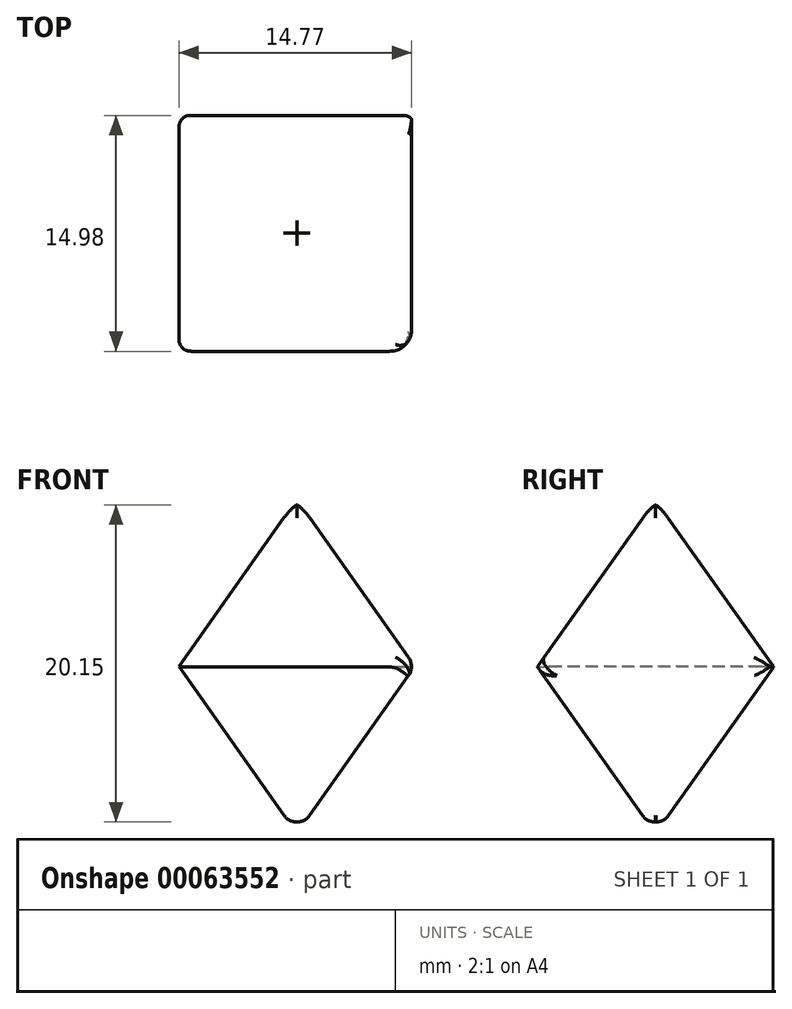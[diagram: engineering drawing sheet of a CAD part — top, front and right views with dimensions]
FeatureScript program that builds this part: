
annotation { "Feature Type Name" : "Feature", "Feature Type Description" : "" }
export const myFeature = defineFeature(function(context is Context, id is Id, definition is map)
    precondition{}
    {
        {
            var Q0;
            Q0=qCreatedBy(makeId("Top.planeOp"),FACE);
            var sketch = newSketch(context, id + "F0", { "sketchPlane" : qUnion([Q0])});
            skLineSegment(sketch, "E0", {"start": v(-43.73, 28.18) * mm, "end": v(-28.73, 28.18) * mm});
            skLineSegment(sketch, "E1", {"start": v(-43.73, 28.18) * mm, "end": v(-43.73, 43.18) * mm});
            skLineSegment(sketch, "E2", {"start": v(-43.73, 43.18) * mm, "end": v(-28.73, 43.18) * mm});
            skLineSegment(sketch, "E3", {"start": v(-28.73, 43.18) * mm, "end": v(-28.73, 28.18) * mm});
            skSolve(sketch);
        }
        {
            var Q0;
            Q0 = qSketchRegion(id + "F0", true);
            extrude(context, id + "F1", {"entities" : qUnion([Q0]), "depth" : 30 * mm, "hasSecondDirection" : true, "secondDirectionOppositeDirection" : true, "secondDirectionDepth" : 25 * mm});
        }
        {
            var Q0;
            Q0=qCreatedBy(makeId("Right.planeOp"),FACE);
            var sketch = newSketch(context, id + "F2", { "sketchPlane" : qUnion([Q0])});
            skLineSegment(sketch, "E4", {"start": v(67.65, 0) * mm, "end": v(67.65, 10) * mm});
            skLineSegment(sketch, "E5", {"start": v(43.2, 10) * mm, "end": v(28.2, 10) * mm});
            skLineSegment(sketch, "E6", {"start": v(35.7, 10) * mm, "end": v(35.7, 20.6) * mm});
            skPoint(sketch, "E6.endSnap0", {"position": v(35.7, 10) * mm});
            skLineSegment(sketch, "E7", {"start": v(43.2, 10) * mm, "end": v(35.7, 20.6) * mm});
            skLineSegment(sketch, "E8", {"start": v(28.2, 10) * mm, "end": v(35.7, 20.6) * mm});
            skLineSegment(sketch, "E9", {"start": v(35.7, 10) * mm, "end": v(35.7, -0.6) * mm});
            skLineSegment(sketch, "E10", {"start": v(43.2, 10) * mm, "end": v(35.7, -0.6) * mm});
            skLineSegment(sketch, "E11", {"start": v(28.2, 10) * mm, "end": v(35.7, -0.6) * mm});
            skLineSegment(sketch, "E12", {"start": v(61.06, 3.69) * mm, "end": v(59.34, 37.87) * mm});
            skLineSegment(sketch, "E13", {"start": v(59.34, 37.87) * mm, "end": v(23.65, 37.87) * mm});
            skLineSegment(sketch, "E14", {"start": v(23.65, 37.87) * mm, "end": v(21.08, -33.5) * mm});
            skLineSegment(sketch, "E15", {"start": v(21.08, -33.5) * mm, "end": v(56.54, -31.78) * mm});
            skLineSegment(sketch, "E16", {"start": v(56.54, -31.78) * mm, "end": v(61.06, 3.69) * mm});
            skSolve(sketch);
        }
        {
            var Q0;
            Q0=makeQuery(id+"F2.imprint","IMPRINT",FACE,{"disambiguationData":[TD([[makeQuery(id+"F2.imprint","IMPRINT",EDGE,{"derivedFrom":sQuery(id+"F2.wireOp",EDGE,"E7")}),-1.0]])]});
            extrude(context, id + "F3", {"entities" : qUnion([Q0]), "operationType" : NewBodyOperationType.REMOVE, "oppositeDirection" : true, "depth" : 61.9 * mm});
        }
        {
            var Q0;
            Q0=qCreatedBy(makeId("Front.planeOp"),FACE);
            var sketch = newSketch(context, id + "F4", { "sketchPlane" : qUnion([Q0])});
            skLineSegment(sketch, "E17", {"start": v(-28.74, 10.03) * mm, "end": v(-43.74, 10.03) * mm});
            skLineSegment(sketch, "E18", {"start": v(-36.24, 10.03) * mm, "end": v(-36.24, 20.63) * mm});
            skLineSegment(sketch, "E19", {"start": v(-36.24, 10.03) * mm, "end": v(-36.24, -0.58) * mm});
            skLineSegment(sketch, "E20", {"start": v(-36.24, 20.63) * mm, "end": v(-28.74, 10.03) * mm});
            skLineSegment(sketch, "E21", {"start": v(-36.24, -0.58) * mm, "end": v(-43.74, 10.03) * mm});
            skLineSegment(sketch, "E22", {"start": v(-43.74, 10.03) * mm, "end": v(-36.24, 20.63) * mm});
            skLineSegment(sketch, "E23", {"start": v(-28.74, 10.03) * mm, "end": v(-36.24, -0.58) * mm});
            skLineSegment(sketch, "E24", {"start": v(-47.6, -2.2) * mm, "end": v(-47.6, 22.43) * mm});
            skLineSegment(sketch, "E25", {"start": v(-47.6, 22.43) * mm, "end": v(-25.78, 22.43) * mm});
            skLineSegment(sketch, "E26", {"start": v(-25.78, 22.43) * mm, "end": v(-25.78, -2.05) * mm});
            skLineSegment(sketch, "E27", {"start": v(-25.78, -2.05) * mm, "end": v(-47.6, -2.2) * mm});
            skSolve(sketch);
        }
        {
            var Q0;
            Q0=makeQuery(id+"F4.imprint","IMPRINT",FACE,{"disambiguationData":[TD([[makeQuery(id+"F4.imprint","IMPRINT",EDGE,{"derivedFrom":sQuery(id+"F4.wireOp",EDGE,"E20")}),1.0]])]});
            extrude(context, id + "F5", {"entities" : qUnion([Q0]), "operationType" : NewBodyOperationType.REMOVE, "oppositeDirection" : true, "depth" : 47.86 * mm});
        }
        {
            var Q0;
            Q0=makeQuery(id+"F5.boolean.opBoolean","INTERSECT",EDGE,{"derivedFrom":[makeQuery(id+"F3.boolean.opBoolean","COPY",FACE,{"derivedFrom":makeQuery(id+"F3.opExtrude","SWEPT_FACE",FACE,{"disambiguationData":[OSD([sQuery(id+"F2.wireOp",EDGE,"E8")])]})}),makeQuery(id+"F5.opExtrude","SWEPT_FACE",FACE,{"disambiguationData":[OSD([sQuery(id+"F4.wireOp",EDGE,"E20")])]})]});
            var Q1;
            Q1=makeQuery(id+"F5.boolean.opBoolean","INTERSECT",EDGE,{"derivedFrom":[makeQuery(id+"F3.boolean.opBoolean","COPY",FACE,{"derivedFrom":makeQuery(id+"F3.opExtrude","SWEPT_FACE",FACE,{"disambiguationData":[OSD([sQuery(id+"F2.wireOp",EDGE,"E10")])]})}),makeQuery(id+"F5.opExtrude","SWEPT_FACE",FACE,{"disambiguationData":[OSD([sQuery(id+"F4.wireOp",EDGE,"E23")])]})]});
            var Q2;
            Q2=makeQuery(id+"F5.boolean.opBoolean","COPY",FACE,{"derivedFrom":makeQuery(id+"F5.opExtrude","SWEPT_FACE",FACE,{"disambiguationData":[OSD([sQuery(id+"F4.wireOp",EDGE,"E23")])]})});
            var Q3;
            Q3=makeQuery(id+"F5.boolean.opBoolean","INTERSECT",EDGE,{"derivedFrom":[makeQuery(id+"F3.boolean.opBoolean","COPY",FACE,{"derivedFrom":makeQuery(id+"F3.opExtrude","SWEPT_FACE",FACE,{"disambiguationData":[OSD([sQuery(id+"F2.wireOp",EDGE,"E7")])]})}),makeQuery(id+"F5.opExtrude","SWEPT_FACE",FACE,{"disambiguationData":[OSD([sQuery(id+"F4.wireOp",EDGE,"E20")])]})]});
            var Q4;
            Q4=makeQuery(id+"F5.boolean.opBoolean","INTERSECT",EDGE,{"derivedFrom":[makeQuery(id+"F3.boolean.opBoolean","COPY",FACE,{"derivedFrom":makeQuery(id+"F3.opExtrude","SWEPT_FACE",FACE,{"disambiguationData":[OSD([sQuery(id+"F2.wireOp",EDGE,"E7")])]})}),makeQuery(id+"F5.opExtrude","SWEPT_FACE",FACE,{"disambiguationData":[OSD([sQuery(id+"F4.wireOp",EDGE,"E22")])]})]});
            var Q5;
            Q5=makeQuery(id+"F5.boolean.opBoolean","INTERSECT",EDGE,{"derivedFrom":[makeQuery(id+"F3.boolean.opBoolean","COPY",FACE,{"derivedFrom":makeQuery(id+"F3.opExtrude","SWEPT_FACE",FACE,{"disambiguationData":[OSD([sQuery(id+"F2.wireOp",EDGE,"E10")])]})}),makeQuery(id+"F5.opExtrude","SWEPT_FACE",FACE,{"disambiguationData":[OSD([sQuery(id+"F4.wireOp",EDGE,"E21")])]})]});
            var Q6;
            Q6=makeQuery(id+"F5.boolean.opBoolean","INTERSECT",EDGE,{"derivedFrom":[makeQuery(id+"F3.boolean.opBoolean","COPY",FACE,{"derivedFrom":makeQuery(id+"F3.opExtrude","SWEPT_FACE",FACE,{"disambiguationData":[OSD([sQuery(id+"F2.wireOp",EDGE,"E11")])]})}),makeQuery(id+"F5.opExtrude","SWEPT_FACE",FACE,{"disambiguationData":[OSD([sQuery(id+"F4.wireOp",EDGE,"E23")])]})]});
            var Q7;
            Q7=makeQuery(id+"F5.boolean.opBoolean","INTERSECT",EDGE,{"derivedFrom":[makeQuery(id+"F3.boolean.opBoolean","COPY",FACE,{"derivedFrom":makeQuery(id+"F3.opExtrude","SWEPT_FACE",FACE,{"disambiguationData":[OSD([sQuery(id+"F2.wireOp",EDGE,"E11")])]})}),makeQuery(id+"F5.opExtrude","SWEPT_FACE",FACE,{"disambiguationData":[OSD([sQuery(id+"F4.wireOp",EDGE,"E21")])]})]});
            var Q8;
            Q8=makeQuery(id+"F5.boolean.opBoolean","INTERSECT",EDGE,{"derivedFrom":[makeQuery(id+"F3.boolean.opBoolean","COPY",FACE,{"derivedFrom":makeQuery(id+"F3.opExtrude","SWEPT_FACE",FACE,{"disambiguationData":[OSD([sQuery(id+"F2.wireOp",EDGE,"E8")])]})}),makeQuery(id+"F5.opExtrude","SWEPT_FACE",FACE,{"disambiguationData":[OSD([sQuery(id+"F4.wireOp",EDGE,"E22")])]})]});
            fillet(context, id + "F6", {"entities" : qUnion([Q0, Q1, Q2, Q3, Q4, Q5, Q6, Q7, Q8]), "radius" : 1 * mm, "tangentPropagation" : true, "allowEdgeOverflow" : false});
        }
    });
